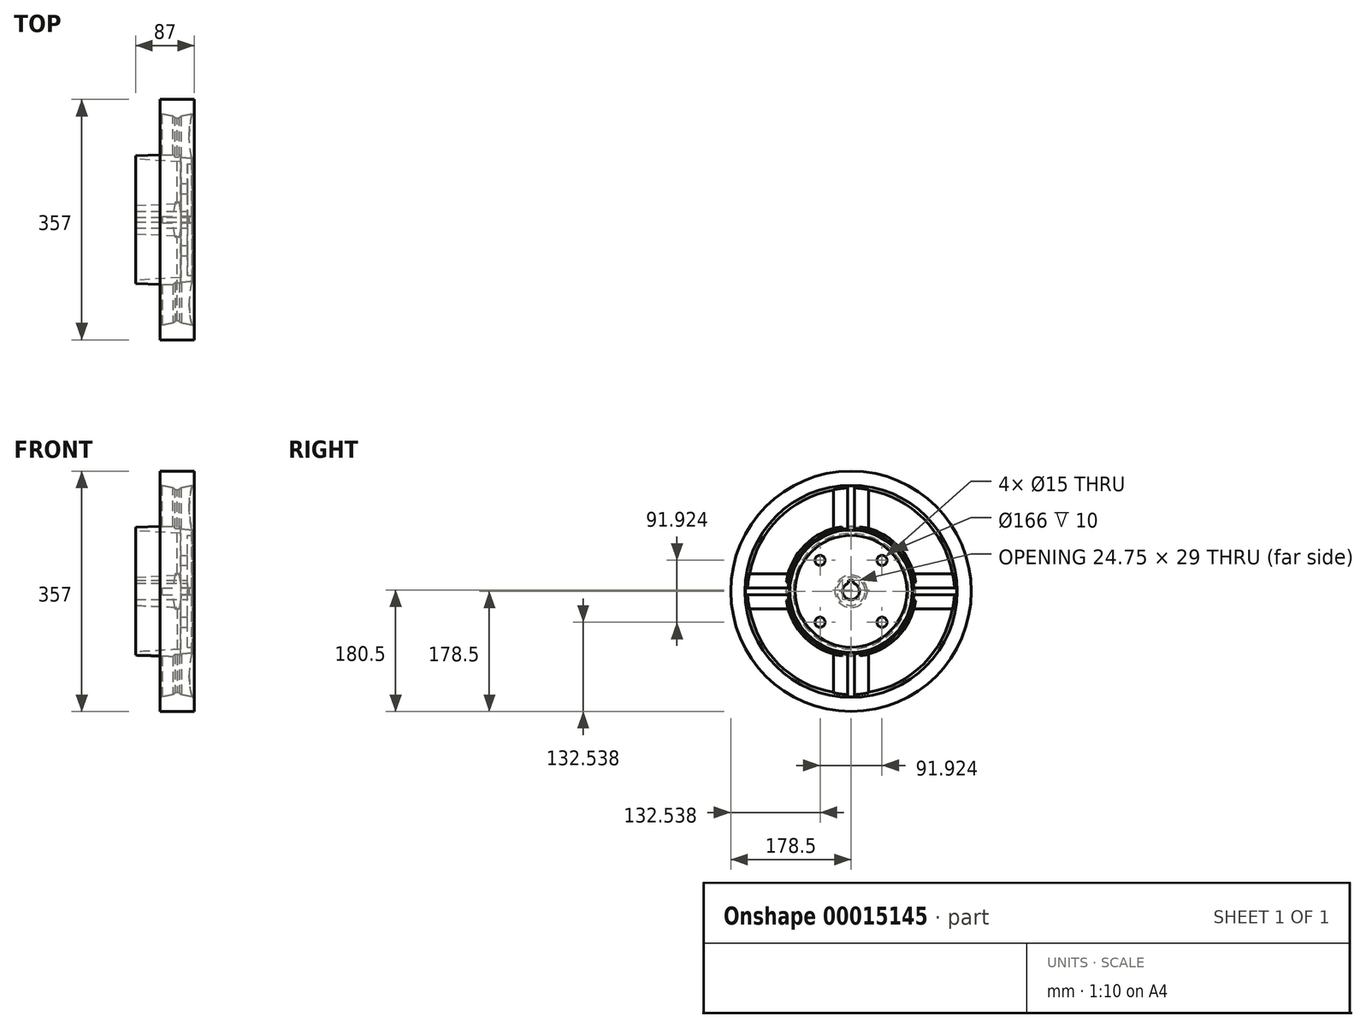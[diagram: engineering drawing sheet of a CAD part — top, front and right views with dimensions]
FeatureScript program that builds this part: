
annotation { "Feature Type Name" : "Feature", "Feature Type Description" : "" }
export const myFeature = defineFeature(function(context is Context, id is Id, definition is map)
    precondition{}
    {
        {
            var Q0;
            Q0=qCreatedBy(makeId("Front.planeOp"),FACE);
            var sketch = newSketch(context, id + "F0", { "sketchPlane" : qUnion([Q0])});
            skLineSegment(sketch, "E0", {"start": v(51.53, 0) * mm, "end": v(-105.64, 0) * mm, "construction": true});
            skLineSegment(sketch, "E1", {"start": v(0, 12.5) * mm, "end": v(-77, 12.5) * mm});
            skLineSegment(sketch, "E2", {"start": v(-77, 12.5) * mm, "end": v(-77, 21) * mm});
            skLineSegment(sketch, "E3", {"start": v(-77, 21) * mm, "end": v(-10, 24) * mm});
            skLineSegment(sketch, "E4", {"start": v(-10, 24) * mm, "end": v(-10, 86) * mm});
            skLineSegment(sketch, "E5", {"start": v(-10, 86) * mm, "end": v(-77, 90) * mm});
            skLineSegment(sketch, "E6", {"start": v(-77, 90) * mm, "end": v(-77, 95) * mm});
            skLineSegment(sketch, "E7", {"start": v(-77, 95) * mm, "end": v(-10.5, 97) * mm});
            skLineSegment(sketch, "E8", {"start": v(-10.5, 97) * mm, "end": v(-10.5, 93) * mm});
            skLineSegment(sketch, "E9", {"start": v(-10.5, 93) * mm, "end": v(10, 91) * mm});
            skLineSegment(sketch, "E10", {"start": v(10, 91) * mm, "end": v(10, 83) * mm});
            skLineSegment(sketch, "E11", {"start": v(10, 83) * mm, "end": v(0, 83) * mm});
            skLineSegment(sketch, "E12", {"start": v(0, 83) * mm, "end": v(0, 12.5) * mm});
            skLineSegment(sketch, "E13", {"start": v(10, 157.5) * mm, "end": v(10, 178.5) * mm});
            skLineSegment(sketch, "E14", {"start": v(10, 178.5) * mm, "end": v(-41, 178.5) * mm});
            skLineSegment(sketch, "E15", {"start": v(-41, 178.5) * mm, "end": v(-41, 157.5) * mm});
            skLineSegment(sketch, "E16", {"start": v(-41, 157.5) * mm, "end": v(-15.5, 152.5) * mm});
            skLineSegment(sketch, "E17", {"start": v(-15.5, 152.5) * mm, "end": v(10, 157.5) * mm});
            skLineSegment(sketch, "E18", {"start": v(10, 157.5) * mm, "end": v(10, 91) * mm, "construction": true});
            skLineSegment(sketch, "E19", {"start": v(-15.5, 178.5) * mm, "end": v(-15.5, 96.85) * mm, "construction": true});
            skLineSegment(sketch, "E20.0", {"start": v(-20.5, 153.48) * mm, "end": v(-20.5, 96.22) * mm});
            skLineSegment(sketch, "E21.0", {"start": v(-10.5, 153.48) * mm, "end": v(-10.5, 97) * mm});
            skArc(sketch, "E22", {"start": v(10, 157.5) * mm, "mid": v(5.87, 124.25) * mm, "end": v(10, 91) * mm});
            skLineSegment(sketch, "E23", {"start": v(-36.5, 156.62) * mm, "end": v(-36.5, 96.22) * mm});
            skLineSegment(sketch, "E24", {"start": v(-56.23, 124) * mm, "end": v(156.47, 124) * mm, "construction": true});
            skSolve(sketch);
        }
        {
            var Q0;
            Q0=makeQuery(id+"F0.imprint","IMPRINT",FACE,{"disambiguationData":[TD([[makeQuery(id+"F0.imprint","IMPRINT",EDGE,{"derivedFrom":sQuery(id+"F0.wireOp",EDGE,"E1")}),-1.0]])]});
            var Q1;
            {var subQ7=sQuery(id+"F0.wireOp",EDGE,"E13");Q1=makeQuery(id+"F0.imprint","IMPRINT",FACE,{"disambiguationData":[TD([[makeQuery(id+"F0.imprint","IMPRINT",EDGE,{"derivedFrom":subQ7}),1.0]])]});}
            var Q2;
            Q2=sQuery(id+"F0.wireOp",EDGE,"E0");
            revolve(context, id + "F1", {"entities" : qUnion([Q0, Q1]), "axis" : qUnion([Q2]), "revolveType" : RevolveType.FULL});
        }
        {
            var Q0;
            Q0=makeQuery(id+"F1.opRevolve","SWEPT_FACE",FACE,{"disambiguationData":[OSD([sQuery(id+"F0.wireOp",EDGE,"E12")])]});
            var sketch = newSketch(context, id + "F2", { "sketchPlane" : qUnion([Q0])});
            skLineSegment(sketch, "E25", {"start": v(0, 0) * mm, "end": v(0, 155.84) * mm, "construction": true});
            skLineSegment(sketch, "E26", {"start": v(131.91, 131.91) * mm, "end": v(0, 0) * mm, "construction": true});
            skCircle(sketch, "E27", {"center": v(0, 0) * mm, "radius": 65 * mm, "construction": true});
            skCircle(sketch, "E28", {"center": v(45.96, 45.96) * mm, "radius": 7.5 * mm});
            skCircle(sketch, "E29.1.0", {"center": v(-45.96, 45.96) * mm, "radius": 7.5 * mm});
            skCircle(sketch, "E29.2.0", {"center": v(-45.96, -45.96) * mm, "radius": 7.5 * mm});
            skCircle(sketch, "E29.3.0", {"center": v(45.96, -45.96) * mm, "radius": 7.5 * mm});
            skSolve(sketch);
        }
        {
            var Q0;
            Q0=makeQuery(id+"F2.imprint","IMPRINT",FACE,{"disambiguationData":[TD([[makeQuery(id+"F2.imprint","IMPRINT",EDGE,{"derivedFrom":sQuery(id+"F2.wireOp",EDGE,"E28")}),1.0]])]});
            var Q1;
            Q1=makeQuery(id+"F2.imprint","IMPRINT",FACE,{"disambiguationData":[TD([[makeQuery(id+"F2.imprint","IMPRINT",EDGE,{"derivedFrom":sQuery(id+"F2.wireOp",EDGE,"E29.1.0")}),1.0]])]});
            var Q2;
            Q2=makeQuery(id+"F2.imprint","IMPRINT",FACE,{"disambiguationData":[TD([[makeQuery(id+"F2.imprint","IMPRINT",EDGE,{"derivedFrom":sQuery(id+"F2.wireOp",EDGE,"E29.2.0")}),1.0]])]});
            var Q3;
            Q3=makeQuery(id+"F2.imprint","IMPRINT",FACE,{"disambiguationData":[TD([[makeQuery(id+"F2.imprint","IMPRINT",EDGE,{"derivedFrom":sQuery(id+"F2.wireOp",EDGE,"E29.3.0")}),1.0]])]});
            extrude(context, id + "F3", {"entities" : qUnion([Q0, Q1, Q2, Q3]), "operationType" : NewBodyOperationType.REMOVE, "endBound" : BoundingType.UP_TO_NEXT, "oppositeDirection" : true, "depth" : 25 * mm});
        }
        {
            var Q0;
            Q0=qCreatedBy(makeId("Top.planeOp"),FACE);
            cPlane(context, id + "F4", {"entities" : qUnion([Q0]), "cplaneType" : CPlaneType.OFFSET, "offset" : 315 / 2 * mm, "width" : 150 * mm, "height" : 150 * mm});
        }
        {
            var Q0;
            Q0=qCreatedBy(id+"F4.planeOp",FACE);
            var sketch = newSketch(context, id + "F5", { "sketchPlane" : qUnion([Q0])});
            skLineSegment(sketch, "E30", {"start": v(-103.66, 0) * mm, "end": v(35.4, 0) * mm, "construction": true});
            skLineSegment(sketch, "E31", {"start": v(10, -178.5) * mm, "end": v(-41, -178.5) * mm});
            skLineSegment(sketch, "E32", {"start": v(-41, 178.5) * mm, "end": v(10, 178.5) * mm});
            skLineSegment(sketch, "E33", {"start": v(-15.5, -178.5) * mm, "end": v(-15.5, 178.5) * mm, "construction": true});
            skLineSegment(sketch, "E34.bottom", {"start": v(-37.5, -5) * mm, "end": v(-22, -5) * mm});
            skLineSegment(sketch, "E34.top", {"start": v(-37.5, 5) * mm, "end": v(-22, 5) * mm});
            skLineSegment(sketch, "E34.left", {"start": v(-37.5, -5) * mm, "end": v(-37.5, 5) * mm});
            skLineSegment(sketch, "E34.right", {"start": v(6.5, -5) * mm, "end": v(6.5, 5) * mm});
            skLineSegment(sketch, "E35", {"start": v(-22, 5) * mm, "end": v(-18.5, 26) * mm});
            skLineSegment(sketch, "E36", {"start": v(-18.5, 26) * mm, "end": v(-12.5, 26) * mm});
            skLineSegment(sketch, "E37", {"start": v(-12.5, 26) * mm, "end": v(-9, 5) * mm});
            skLineSegment(sketch, "E38.0.MirrorCS", {"start": v(-22, -5) * mm, "end": v(-18.5, -26) * mm});
            skLineSegment(sketch, "E39.0.MirrorCS", {"start": v(-12.5, -26) * mm, "end": v(-9, -5) * mm});
            skLineSegment(sketch, "E40.0.MirrorCS", {"start": v(-18.5, -26) * mm, "end": v(-12.5, -26) * mm});
            skLineSegment(sketch, "E41.trimOffspring", {"start": v(-9, -5) * mm, "end": v(6.5, -5) * mm});
            skLineSegment(sketch, "E42.trimOffspring", {"start": v(-9, 5) * mm, "end": v(6.5, 5) * mm});
            skSolve(sketch);
        }
        {
            var Q0;
            Q0=makeQuery(id+"F5.imprint","IMPRINT",FACE,{"disambiguationData":[TD([[makeQuery(id+"F5.imprint","IMPRINT",EDGE,{"derivedFrom":sQuery(id+"F5.wireOp",EDGE,"E34.bottom")}),1.0]])]});
            var Q1;
            Q1=makeQuery(id+"F1.opRevolve","SWEPT_FACE",FACE,{"disambiguationData":[OSD([sQuery(id+"F0.wireOp",EDGE,"E7")])]});
            extrude(context, id + "F6", {"entities" : qUnion([Q0]), "endBound" : BoundingType.UP_TO_BODY, "oppositeDirection" : true, "endBoundEntityBody" : qUnion([Q1]), "depth" : 25 * mm});
        }
        {
            var Q0;
            Q0=makeQuery(id+"F6.opExtrude","SWEPT_BODY",BODY,{"disambiguationData":[OSD([sQuery(id+"F5.wireOp",EDGE,"E34.bottom"),sQuery(id+"F5.wireOp",EDGE,"E34.top"),sQuery(id+"F5.wireOp",EDGE,"E34.left"),sQuery(id+"F5.wireOp",EDGE,"E34.right"),sQuery(id+"F5.wireOp",EDGE,"E35"),sQuery(id+"F5.wireOp",EDGE,"E36"),sQuery(id+"F5.wireOp",EDGE,"E37"),sQuery(id+"F5.wireOp",EDGE,"E38.0.MirrorCS"),sQuery(id+"F5.wireOp",EDGE,"E39.0.MirrorCS"),sQuery(id+"F5.wireOp",EDGE,"E40.0.MirrorCS"),sQuery(id+"F5.wireOp",EDGE,"E41.trimOffspring"),sQuery(id+"F5.wireOp",EDGE,"E42.trimOffspring")])]});
            var Q1;
            Q1=makeQuery(id+"F1.opRevolve","SWEPT_FACE",FACE,{"disambiguationData":[OSD([sQuery(id+"F0.wireOp",EDGE,"E1")])]});
            circularPattern(context, id + "F7", {"operationType" : NewBodyOperationType.ADD, "entities" : qUnion([Q0]), "axis" : qUnion([Q1]), "angle" : 360 * degree, "instanceCount" : round(4), "equalSpace" : true});
        }
        {
            var Q0;
            Q0=qCreatedBy(makeId("Top.planeOp"),FACE);
            var sketch = newSketch(context, id + "F8", { "sketchPlane" : qUnion([Q0])});
            skLineSegment(sketch, "E43.0", {"start": v(6.5, 91.2) * mm, "end": v(6.5, 156.73) * mm});
            skArc(sketch, "E44", {"start": v(6.5, 156.73) * mm, "mid": v(2.5, 123.97) * mm, "end": v(6.5, 91.2) * mm});
            skSolve(sketch);
        }
        {
            var Q0;
            Q0=makeQuery(id+"F8.imprint","IMPRINT",FACE,{"disambiguationData":[TD([[makeQuery(id+"F8.imprint","IMPRINT",EDGE,{"derivedFrom":sQuery(id+"F8.wireOp",EDGE,"E43.0")}),1.0]])]});
            var Q1;
            Q1=makeQuery(id+"F1.opRevolve","SWEPT_FACE",FACE,{"disambiguationData":[OSD([sQuery(id+"F0.wireOp",EDGE,"E9")])]});
            revolve(context, id + "F9", {"operationType" : NewBodyOperationType.REMOVE, "entities" : qUnion([Q0]), "axis" : qUnion([Q1]), "revolveType" : RevolveType.FULL, "oppositeDirection" : true});
        }
        {
            var Q0;
            Q0=makeQuery(id+"F1.opRevolve","SWEPT_FACE",FACE,{"disambiguationData":[OSD([sQuery(id+"F0.wireOp",EDGE,"E12")])]});
            var sketch = newSketch(context, id + "F10", { "sketchPlane" : qUnion([Q0])});
            skLineSegment(sketch, "E45", {"start": v(0, 0) * mm, "end": v(0, 62.8) * mm, "construction": true});
            skLineSegment(sketch, "E46.bottom", {"start": v(-3.5, 4.88) * mm, "end": v(3.5, 4.88) * mm});
            skLineSegment(sketch, "E46.top", {"start": v(-3.5, 16.5) * mm, "end": v(3.5, 16.5) * mm});
            skLineSegment(sketch, "E46.left", {"start": v(-3.5, 4.88) * mm, "end": v(-3.5, 16.5) * mm});
            skLineSegment(sketch, "E46.right", {"start": v(3.5, 4.88) * mm, "end": v(3.5, 16.5) * mm});
            skSolve(sketch);
        }
        {
            var Q0;
            {var subQ5=sQuery(id+"F10.wireOp",EDGE,"E46.bottom");Q0=makeQuery(id+"F10.imprint","IMPRINT",FACE,{"disambiguationData":[TD([[makeQuery(id+"F10.imprint","IMPRINT",EDGE,{"derivedFrom":subQ5}),1.0]])]});}
            var Q1;
            {var subQ5=sQuery(id+"F10.wireOp",EDGE,"E46.top");Q1=makeQuery(id+"F10.imprint","IMPRINT",FACE,{"disambiguationData":[TD([[makeQuery(id+"F10.imprint","IMPRINT",EDGE,{"derivedFrom":subQ5}),-1.0]])]});}
            var Q2;
            Q2=makeQuery(id+"F1.opRevolve","SWEPT_FACE",FACE,{"disambiguationData":[OSD([sQuery(id+"F0.wireOp",EDGE,"E2")])]});
            extrude(context, id + "F11", {"entities" : qUnion([Q0, Q1]), "operationType" : NewBodyOperationType.REMOVE, "endBound" : BoundingType.UP_TO_SURFACE, "oppositeDirection" : true, "endBoundEntityFace" : qUnion([Q2]), "depth" : 25 * mm});
        }
    });
